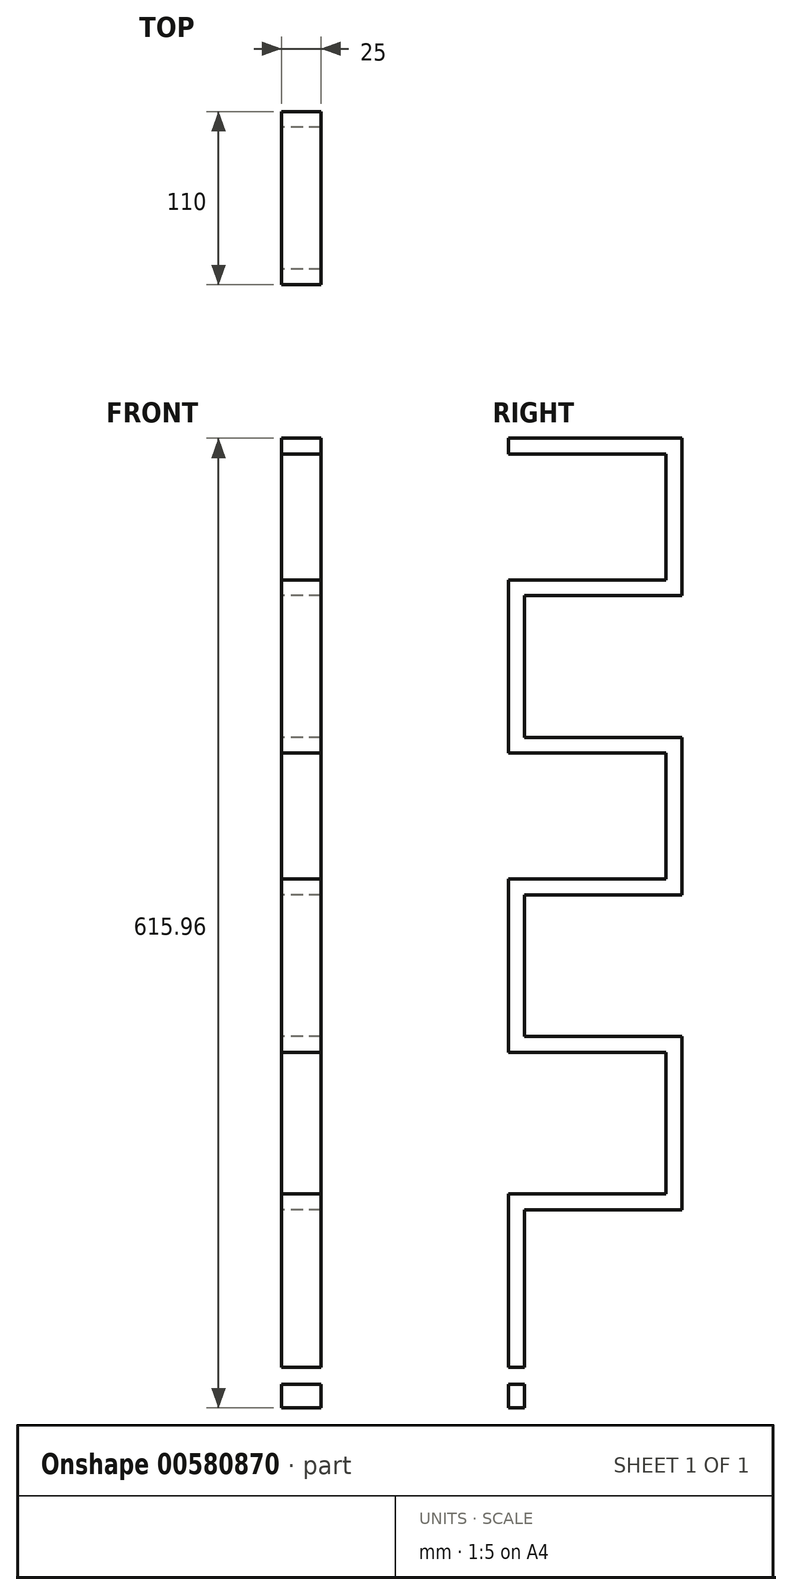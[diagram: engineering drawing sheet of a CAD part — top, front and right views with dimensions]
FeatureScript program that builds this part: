
annotation { "Feature Type Name" : "Feature", "Feature Type Description" : "" }
export const myFeature = defineFeature(function(context is Context, id is Id, definition is map)
    precondition{}
    {
        {
            var Q0;
            Q0=qCreatedBy(makeId("Right.planeOp"),FACE);
            var sketch = newSketch(context, id + "F0", { "sketchPlane" : qUnion([Q0])});
            skLineSegment(sketch, "E0.bottom", {"start": v(-94.4, 133.1) * mm, "end": v(5.6, 133.1) * mm});
            skLineSegment(sketch, "E0.top", {"start": v(-94.4, 123.1) * mm, "end": v(5.6, 123.1) * mm});
            skLineSegment(sketch, "E0.left", {"start": v(-94.4, 133.1) * mm, "end": v(-94.4, 123.1) * mm});
            skLineSegment(sketch, "E1.bottom", {"start": v(5.6, 133.1) * mm, "end": v(15.6, 133.1) * mm});
            skLineSegment(sketch, "E1.top", {"start": v(5.6, 33.1) * mm, "end": v(15.6, 33.1) * mm});
            skLineSegment(sketch, "E1.left", {"start": v(5.6, 123.1) * mm, "end": v(5.6, 43.1) * mm});
            skLineSegment(sketch, "E1.right", {"start": v(15.6, 133.1) * mm, "end": v(15.6, 33.1) * mm});
            skLineSegment(sketch, "E2.bottom", {"start": v(5.6, 33.1) * mm, "end": v(-84.4, 33.1) * mm});
            skLineSegment(sketch, "E2.top", {"start": v(5.6, 43.1) * mm, "end": v(-94.4, 43.1) * mm});
            skLineSegment(sketch, "E2.right", {"start": v(-94.4, 33.1) * mm, "end": v(-94.4, 43.1) * mm});
            skLineSegment(sketch, "E3.top", {"start": v(-94.4, -66.9) * mm, "end": v(-84.4, -66.9) * mm});
            skLineSegment(sketch, "E3.left", {"start": v(-94.4, 33.1) * mm, "end": v(-94.4, -66.9) * mm});
            skLineSegment(sketch, "E3.right", {"start": v(-84.4, 33.1) * mm, "end": v(-84.4, -56.9) * mm});
            skLineSegment(sketch, "E4.bottom", {"start": v(-84.4, -66.9) * mm, "end": v(5.6, -66.9) * mm});
            skLineSegment(sketch, "E4.top", {"start": v(-84.4, -56.9) * mm, "end": v(15.6, -56.9) * mm});
            skLineSegment(sketch, "E4.right", {"start": v(15.6, -66.9) * mm, "end": v(15.6, -56.9) * mm});
            skLineSegment(sketch, "E5.bottom", {"start": v(5.6, -56.9) * mm, "end": v(15.6, -56.9) * mm});
            skLineSegment(sketch, "E5.top", {"start": v(5.6, -156.9) * mm, "end": v(15.6, -156.9) * mm});
            skLineSegment(sketch, "E5.left", {"start": v(5.6, -66.9) * mm, "end": v(5.6, -146.9) * mm});
            skLineSegment(sketch, "E5.right", {"start": v(15.6, -56.9) * mm, "end": v(15.6, -156.9) * mm});
            skLineSegment(sketch, "E6.bottom", {"start": v(5.6, -156.9) * mm, "end": v(-84.4, -156.9) * mm});
            skLineSegment(sketch, "E6.top", {"start": v(5.6, -146.9) * mm, "end": v(-94.4, -146.9) * mm});
            skLineSegment(sketch, "E6.right", {"start": v(-94.4, -156.9) * mm, "end": v(-94.4, -146.9) * mm});
            skLineSegment(sketch, "E7.top", {"start": v(-94.4, -256.9) * mm, "end": v(-84.4, -256.9) * mm});
            skLineSegment(sketch, "E7.left", {"start": v(-94.4, -156.9) * mm, "end": v(-94.4, -256.9) * mm});
            skLineSegment(sketch, "E7.right", {"start": v(-84.4, -156.9) * mm, "end": v(-84.4, -246.9) * mm});
            skLineSegment(sketch, "E8.bottom", {"start": v(-84.4, -256.9) * mm, "end": v(5.6, -256.9) * mm});
            skLineSegment(sketch, "E8.top", {"start": v(-84.4, -246.9) * mm, "end": v(15.6, -246.9) * mm});
            skLineSegment(sketch, "E8.right", {"start": v(15.6, -256.9) * mm, "end": v(15.6, -246.9) * mm});
            skLineSegment(sketch, "E9.top", {"start": v(5.6, -356.9) * mm, "end": v(15.6, -356.9) * mm});
            skLineSegment(sketch, "E9.left", {"start": v(5.6, -256.9) * mm, "end": v(5.6, -346.9) * mm});
            skLineSegment(sketch, "E9.right", {"start": v(15.6, -256.9) * mm, "end": v(15.6, -356.9) * mm});
            skLineSegment(sketch, "E10.bottom", {"start": v(5.6, -356.9) * mm, "end": v(-84.4, -356.9) * mm});
            skLineSegment(sketch, "E10.top", {"start": v(5.6, -346.9) * mm, "end": v(-94.4, -346.9) * mm});
            skLineSegment(sketch, "E10.right", {"start": v(-94.4, -356.9) * mm, "end": v(-94.4, -346.9) * mm});
            skLineSegment(sketch, "E11.top", {"start": v(-94.4, -456.9) * mm, "end": v(-84.4, -456.9) * mm});
            skLineSegment(sketch, "E11.left", {"start": v(-94.4, -356.9) * mm, "end": v(-94.4, -456.9) * mm});
            skLineSegment(sketch, "E11.right", {"start": v(-84.4, -356.9) * mm, "end": v(-84.4, -456.9) * mm});
            skLineSegment(sketch, "E12", {"start": v(-94.4, -467.86) * mm, "end": v(-94.4, -482.86) * mm});
            skLineSegment(sketch, "E13", {"start": v(-84.4, -467.86) * mm, "end": v(-84.4, -482.86) * mm});
            skLineSegment(sketch, "E14.bottom", {"start": v(-94.4, -467.86) * mm, "end": v(-84.4, -467.86) * mm});
            skLineSegment(sketch, "E14.top", {"start": v(-94.4, -482.86) * mm, "end": v(-84.4, -482.86) * mm});
            skSolve(sketch);
        }
        {
            var Q0;
            Q0 = qSketchRegion(id + "F0", true);
            extrude(context, id + "F1", {"entities" : qUnion([Q0]), "depth" : 25 * mm, "offsetDistance" : 25 * mm});
        }
    });
